# Revit family: Evoflat TDV W_RFA_1
name_source: partatom
category: Mechanical Equipment
units: mm (PartAtom-declared; Revit-internal decimal feet)

## family parameters
Always vertical = Yes
Classification = None
Cut with Voids When Loaded = No
OmniClass Number = 23.75.65.11.11
OmniClass Title = Heating Controllers
Part Type = Normal
Room Calculation Point = No
Round Connector Dimension = Use Diameter
Shared = No
Work Plane-Based = No

## types (6) — shared parameters
Connection = G 3/4 Internal Thread
D = 20 mm  [stored 0.0656168 ft]
Description = Flat Station
H = 443 mm  [stored 1.45341 ft]
H1 = 3 mm  [stored 0.00984252 ft]
H2 = 32 mm
H3 = 33 mm
IfcExportAs = IfcFlowController
IfcExportType = EvoFlat TDV W
Insulation Material = Danfoss EPP insulation
L = 310 mm  [stored 1.01706 ft]
L1 = 55 mm  [stored 0.180446 ft]
L1a = 55 mm  [stored 0.180446 ft]
LOD 200 = No
LOD 350 = Yes
Manufacturer = Danfoss
Max Supply Temperature = 95 °C
Nominal Pressure = PN 10
Nut size = 30 mm  [stored 0.0984252 ft]
Type Image = <None>
URL = https://store.danfoss.com
W = 130 mm  [stored 0.426509 ft]
W1 = 40 mm  [stored 0.131234 ft]
Weight = 8.50 kg

## per-type parameters (varying)
| type | DHW Flow Rate Primary | DHW Pressure Loss Primary | DHW Tap Load 50°C | DHW Temperature DHS/DHR | DHW capacity | HEX material | Model | Model Type |
| Evoflat TDV W_Type 1_Cu_145G0350 | 850 l/h | 40 kPa | 15.3 l/min | 65/22 °C | 43 kW | Danfoss Copper | 145G0350 | Evoflat TDV W_Type 1_Cu |
| Evoflat TDV W_Type 3_Cu_145G0352 | 950 l/h | 27 kPa | 18.3 l/min | 65/16 °C | 55 kW | Danfoss Copper | 145G0352 | Evoflat TDV W_Type 3_Cu |
| Evoflat TDV W_Type 2_Cu_145G0351 | 950 l/h | 30 kPa | 17.5 l/min | 65/21 °C | 49 kW | Danfoss Copper | 145G0351 | Evoflat TDV W_Type 2_Cu |
| Evoflat TDV W_Type 1_Sts_145G0355 | 850 l/h | 40 kPa | 15.3 l/min | 65/22 °C | 43 kW | Danfoss Stainless Steel | 145G0355 | Evoflat TDV W_Type 1_Sts |
| Evoflat TDV W_Type 2_Sts_145G0356 | 950 l/h | 30 kPa | 17.5 l/min | 65/21 °C | 49 kW | Danfoss Stainless Steel | 145G0356 | Evoflat TDV W_Type 2_Sts |
| Evoflat TDV W_Type 3_Sts_145G0357 | 950 l/h | 27 kPa | 18.3 l/min | 65/16 °C | 55 kW | Danfoss Stainless Steel | 145G0357 | Evoflat TDV W_Type 3_Sts |

note: [stored X ft] marks values corroborated as IEEE doubles in the binary element streams (Revit-internal decimal feet)

## geometry (parser evidence)
native form markers: Sweep x3
no freeform markers — native parametric forms only
